# Revit family: K-Series Bar Joist-Section
name_source: partatom
category: Detail Items
revit_build: Autodesk Revit Architecture 2012 (Build: 20110210_1515)
units: mm (PartAtom-declared; Revit-internal decimal feet)

## types (64) — shared parameters

## per-type parameters (varying)
| type | Depth | Keynote | Wt |
| 8K1 | 8" | 05 21 00.B1 | 5.1 |
| 10K1 | 10" | 05 21 00.B2 | 5 |
| 12K1 | 12" | 05 21 00.B3 | 5 |
| 12K3 | 12" | 05 21 00.B4 | 5.7 |
| 12K5 | 12" | 05 21 00.B5 | 7.1 |
| 14K1 | 14" | 05 21 00.B6 | 5.2 |
| 14K3 | 14" | 05 21 00.B7 | 6 |
| 14K4 | 14" | 05 21 00.B8 | 6.7 |
| 14K6 | 14" | 05 21 00.B9 | 7.7 |
| 16K2 | 16" | 05 21 00.B10 | 5.5 |
| 16K3 | 16" | 05 21 00.B11 | 6.3 |
| 16K4 | 16" | 05 21 00.B12 | 7 |
| 16K5 | 16" | 05 21 00.B13 | 7.5 |
| 16K6 | 16" | 05 21 00.B14 | 8.1 |
| 16K7 | 16" | 05 21 00.B15 | 8.6 |
| 16K9 | 16" | 05 21 00.B16 | 10 |
| 18K3 | 18" | 05 21 00.B17 | 6.6 |
| 18K4 | 18" | 05 21 00.B18 | 7.2 |
| 18K5 | 18" | 05 21 00.B19 | 7.7 |
| 18K6 | 18" | 05 21 00.B20 | 8.5 |
| 18K7 | 18" | 05 21 00.B21 | 9 |
| 18K9 | 18" | 05 21 00.B22 | 10.2 |
| 18K10 | 18" | 05 21 00.B23 | 11.7 |
| 20K3 | 20" | 05 21 00.B24 | 6.7 |
| 20K4 | 20" | 05 21 00.B25 | 7.6 |
| 20K5 | 20" | 05 21 00.B26 | 8.2 |
| 20K6 | 20" | 05 21 00.B27 | 8.9 |
| 20K7 | 20" | 05 21 00.B28 | 9.3 |
| 20K9 | 20" | 05 21 00.B29 | 10.8 |
| 20K10 | 20" | 05 21 00.B30 | 12.2 |
| 22K4 | 22" | 05 21 00.B31 | 8 |
| 22K5 | 22" | 05 21 00.B32 | 8.8 |
| 22K6 | 22" | 05 21 00.B33 | 9.2 |
| 22K7 | 22" | 05 21 00.B34 | 9.7 |
| 22K9 | 22" | 05 21 00.B35 | 11.3 |
| 22K10 | 22" | 05 21 00.B36 | 12.6 |
| 22K11 | 22" | 05 21 00.B37 | 13.8 |
| 24K4 | 24" | 05 21 00.B38 | 8.4 |
| 24K5 | 24" | 05 21 00.B39 | 9.3 |
| 24K6 | 24" | 05 21 00.B40 | 9.7 |
| 24K7 | 24" | 05 21 00.B41 | 10.1 |
| 24K8 | 24" | 05 21 00.B42 | 11.5 |
| 24K9 | 24" | 05 21 00.B43 | 12 |
| 24K10 | 24" | 05 21 00.B44 | 13.2 |
| 24K12 | 24" | 05 21 00.B45 | 16 |
| 26K5 | 26" | 05 21 00.B46 | 9.8 |
| 26K6 | 26" | 05 21 00.B47 | 10.6 |
| 26K7 | 26" | 05 21 00.B48 | 10.9 |
| 26K8 | 26" | 05 21 00.B49 | 12.1 |
| 26K9 | 26" | 05 21 00.B50 | 12.2 |
| 26K10 | 26" | 05 21 00.B51 | 13.8 |
| 26K12 | 26" | 05 21 00.B52 | 16.6 |
| 28K6 | 28" | 05 21 00.B53 | 11.4 |
| 28K7 | 28" | 05 21 00.B54 | 11.8 |
| 28K8 | 28" | 05 21 00.B55 | 12.7 |
| 28K9 | 28" | 05 21 00.B56 | 13 |
| 28K10 | 28" | 05 21 00.B57 | 14.3 |
| 28K12 | 28" | 05 21 00.B58 | 17.1 |
| 30K7 | 30" | 05 21 00.B59 | 12.3 |
| 30K8 | 30" | 05 21 00.B60 | 13.2 |
| 30K9 | 30" | 05 21 00.B61 | 13.4 |
| 30K10 | 30" | 05 21 00.B62 | 15 |
| 30K11 | 30" | 05 21 00.B63 | 16.4 |
| 30K12 | 30" | 05 21 00.B64 | 17.6 |
